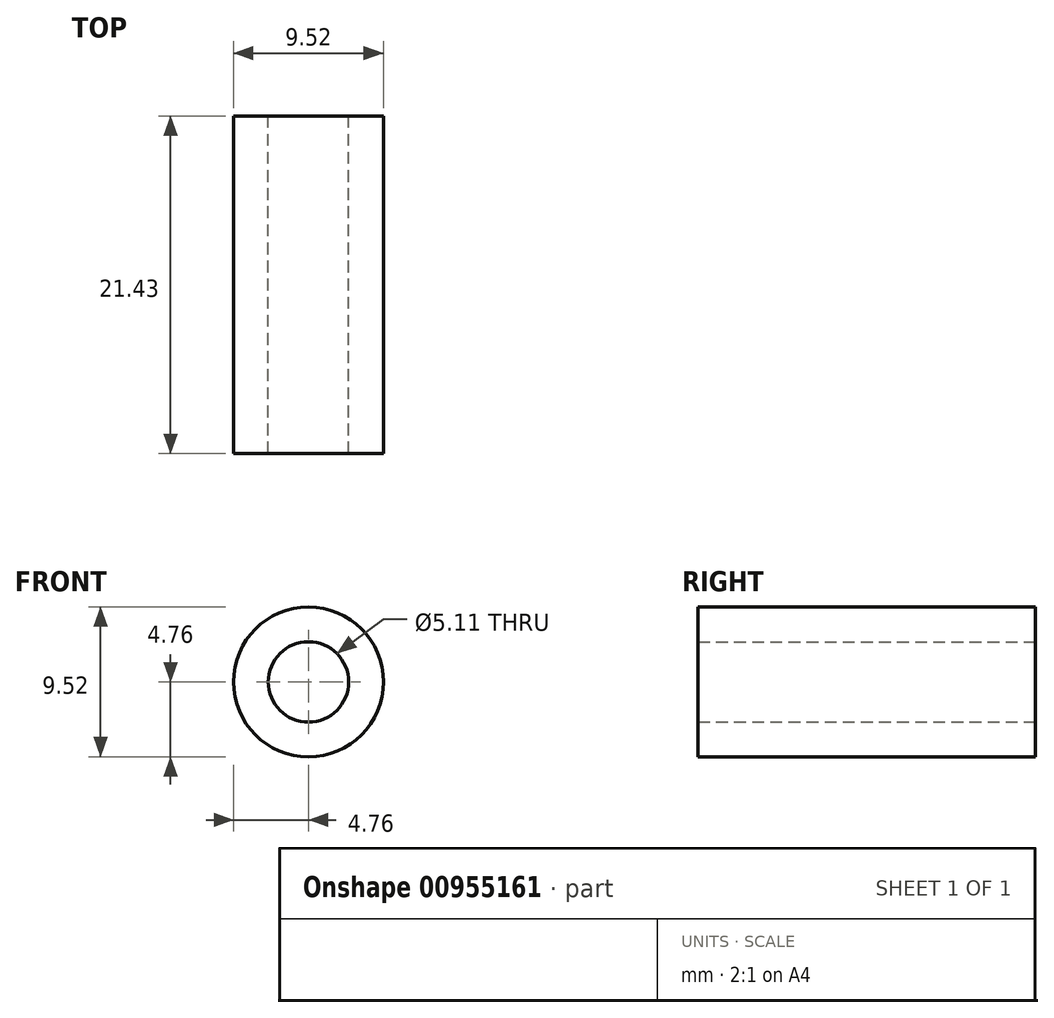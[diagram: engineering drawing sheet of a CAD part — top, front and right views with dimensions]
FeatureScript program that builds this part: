
annotation { "Feature Type Name" : "Feature", "Feature Type Description" : "" }
export const myFeature = defineFeature(function(context is Context, id is Id, definition is map)
    precondition{}
    {
        {
            var Q0;
            Q0=qCreatedBy(makeId("Front.planeOp"),FACE);
            var sketch = newSketch(context, id + "F0", { "sketchPlane" : qUnion([Q0])});
            skCircle(sketch, "E0", {"center": v(0, 0) * mm, "radius": 2.55 * mm});
            skCircle(sketch, "E1", {"center": v(0, 0) * mm, "radius": 4.76 * mm});
            skSolve(sketch);
        }
        {
            var Q0;
            Q0=qSketchRegion(id+"F0",true);
            extrude(context, id + "F1", {"entities" : qUnion([Q0]), "depth" : 21.43 * mm, "offsetDistance" : 25.4 * mm});
        }
    });
